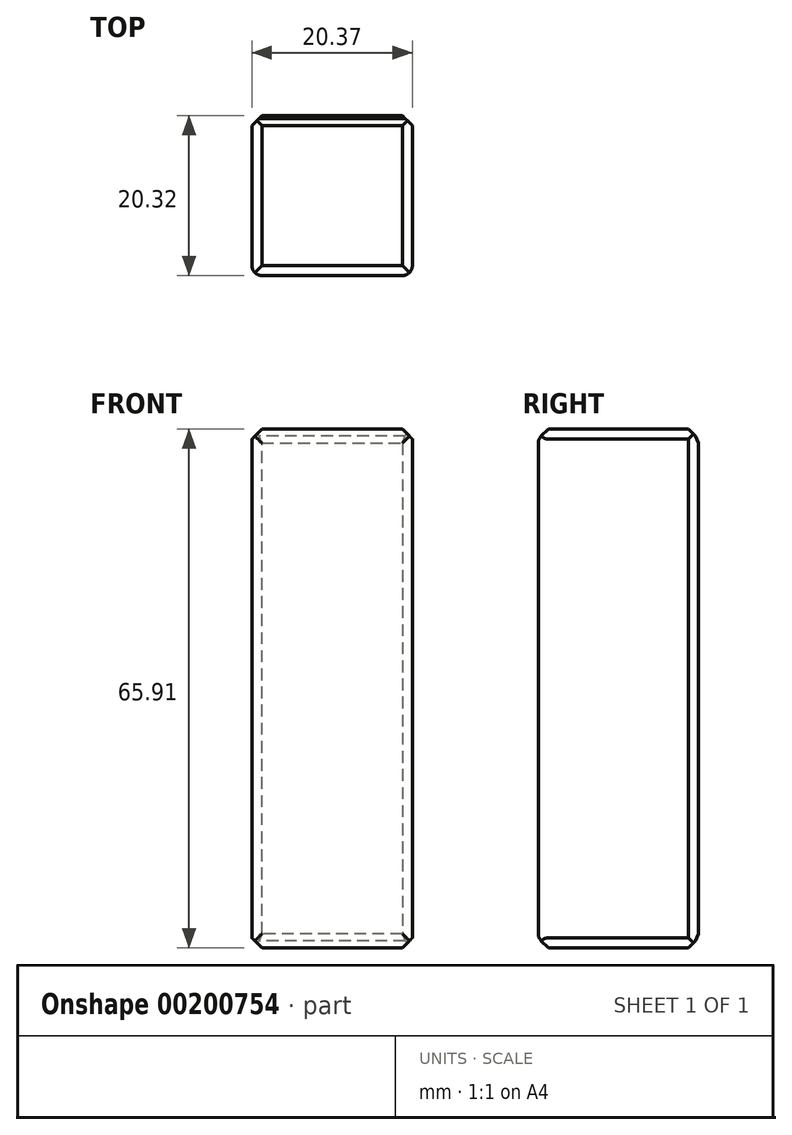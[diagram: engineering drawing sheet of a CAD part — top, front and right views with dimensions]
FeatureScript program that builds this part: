
annotation { "Feature Type Name" : "Feature", "Feature Type Description" : "" }
export const myFeature = defineFeature(function(context is Context, id is Id, definition is map)
    precondition{}
    {
        {
            var Q0;
            Q0=qCreatedBy(makeId("Front.planeOp"),FACE);
            var sketch = newSketch(context, id + "F0", { "sketchPlane" : qUnion([Q0])});
            skLineSegment(sketch, "E0.bottom", {"start": v(0, 43.18) * mm, "end": v(20.37, 43.18) * mm});
            skLineSegment(sketch, "E0.top", {"start": v(0, -22.73) * mm, "end": v(20.37, -22.73) * mm});
            skLineSegment(sketch, "E0.left", {"start": v(0, 43.18) * mm, "end": v(0, -22.73) * mm});
            skLineSegment(sketch, "E0.right", {"start": v(20.37, 43.18) * mm, "end": v(20.37, -22.73) * mm});
            skLineSegment(sketch, "E1.bottom", {"start": v(0.48, 43.18) * mm, "end": v(20.37, 43.18) * mm});
            skSolve(sketch);
        }
        {
            var Q0;
            Q0=makeQuery(id+"F0.imprint","IMPRINT",FACE,{"disambiguationData":[TD([[makeQuery(id+"F0.imprint","IMPRINT",EDGE,{"derivedFrom":sQuery(id+"F0.wireOp",EDGE,"E0.top")}),1.0]])]});
            extrude(context, id + "F1", {"entities" : qUnion([Q0]), "depth" : 20.32 * mm});
        }
        {
            var Q0;
            Q0=makeQuery(id+"F1.opExtrude","SWEPT_FACE",FACE,{"disambiguationData":[OSD([sQuery(id+"F0.wireOp",EDGE,"E0.bottom"),sQuery(id+"F0.wireOp",EDGE,"E1.bottom")])]});
            chamfer(context, id + "F2", {"entities" : qUnion([Q0]), "width" : 1.27 * mm, "tangentPropagation" : true});
        }
        {
            var Q0;
            Q0=makeQuery(id+"F1.opExtrude","SWEPT_FACE",FACE,{"disambiguationData":[OSD([sQuery(id+"F0.wireOp",EDGE,"E0.top")])]});
            chamfer(context, id + "F3", {"entities" : qUnion([Q0]), "width" : 1.27 * mm, "tangentPropagation" : true});
        }
        {
            var Q0;
            Q0=makeQuery(id+"F1.opExtrude","CAP_FACE",FACE,{"disambiguationData":[OSD([sQuery(id+"F0.wireOp",EDGE,"E0.bottom"),sQuery(id+"F0.wireOp",EDGE,"E0.top"),sQuery(id+"F0.wireOp",EDGE,"E0.left"),sQuery(id+"F0.wireOp",EDGE,"E0.right"),sQuery(id+"F0.wireOp",EDGE,"E1.bottom")])],"isStart":true});
            chamfer(context, id + "F4", {"entities" : qUnion([Q0]), "width" : 1.27 * mm, "tangentPropagation" : true});
        }
        {
            var Q0;
            Q0=makeQuery(id+"F1.opExtrude","CAP_FACE",FACE,{"disambiguationData":[OSD([sQuery(id+"F0.wireOp",EDGE,"E0.bottom"),sQuery(id+"F0.wireOp",EDGE,"E0.top"),sQuery(id+"F0.wireOp",EDGE,"E0.left"),sQuery(id+"F0.wireOp",EDGE,"E0.right"),sQuery(id+"F0.wireOp",EDGE,"E1.bottom")])],"isStart":false});
            fillet(context, id + "F5", {"entities" : qUnion([Q0]), "radius" : 1.27 * mm, "tangentPropagation" : true, "allowEdgeOverflow" : false});
        }
    });
